# Revit family: Мойка двухсекционная медицинская из нержавеющей стали
name_source: partatom
category: Оборудование
revit_build: Autodesk Revit 2017 (Build: 20170118_1100(x64)
units: mm (PartAtom-declared; Revit-internal decimal feet)

## family parameters
Всегда вертикально = Да
На основе рабочей плоскости = Нет
Общий = Нет
При загрузке вырезать с полостями = Нет
Размер круглого соединителя = Использовать диаметр
Тип детали = Нормальный
Точка расчета площади = Нет

## types (1)
- Тип
    Общ_Высота = 900 мм
    Общ_Глубина = 600 мм
    Общ_Диаметр ГВ = 13 мм
    Общ_Диаметр К = 50.00 мм
    Общ_Диаметр ХВ = 13 мм
    Общ_Единицы измерения = шт.
    Общ_Масса = 40
    Общ_Наименование = Мойка медицинская двухсекционная из нержавеющей стали в комплекте со смесителем
    Общ_Позиция = 67
    Общ_Поставщик = БТ-Мебель
    Общ_Примечание = Сифон в комплект не входит
    Общ_Тип, марка = БТ-ТНПР/2М-12-С
    Общ_Ширина = 1210 мм

## geometry (parser evidence)
native form markers: Sweep x3
no freeform markers — native parametric forms only
